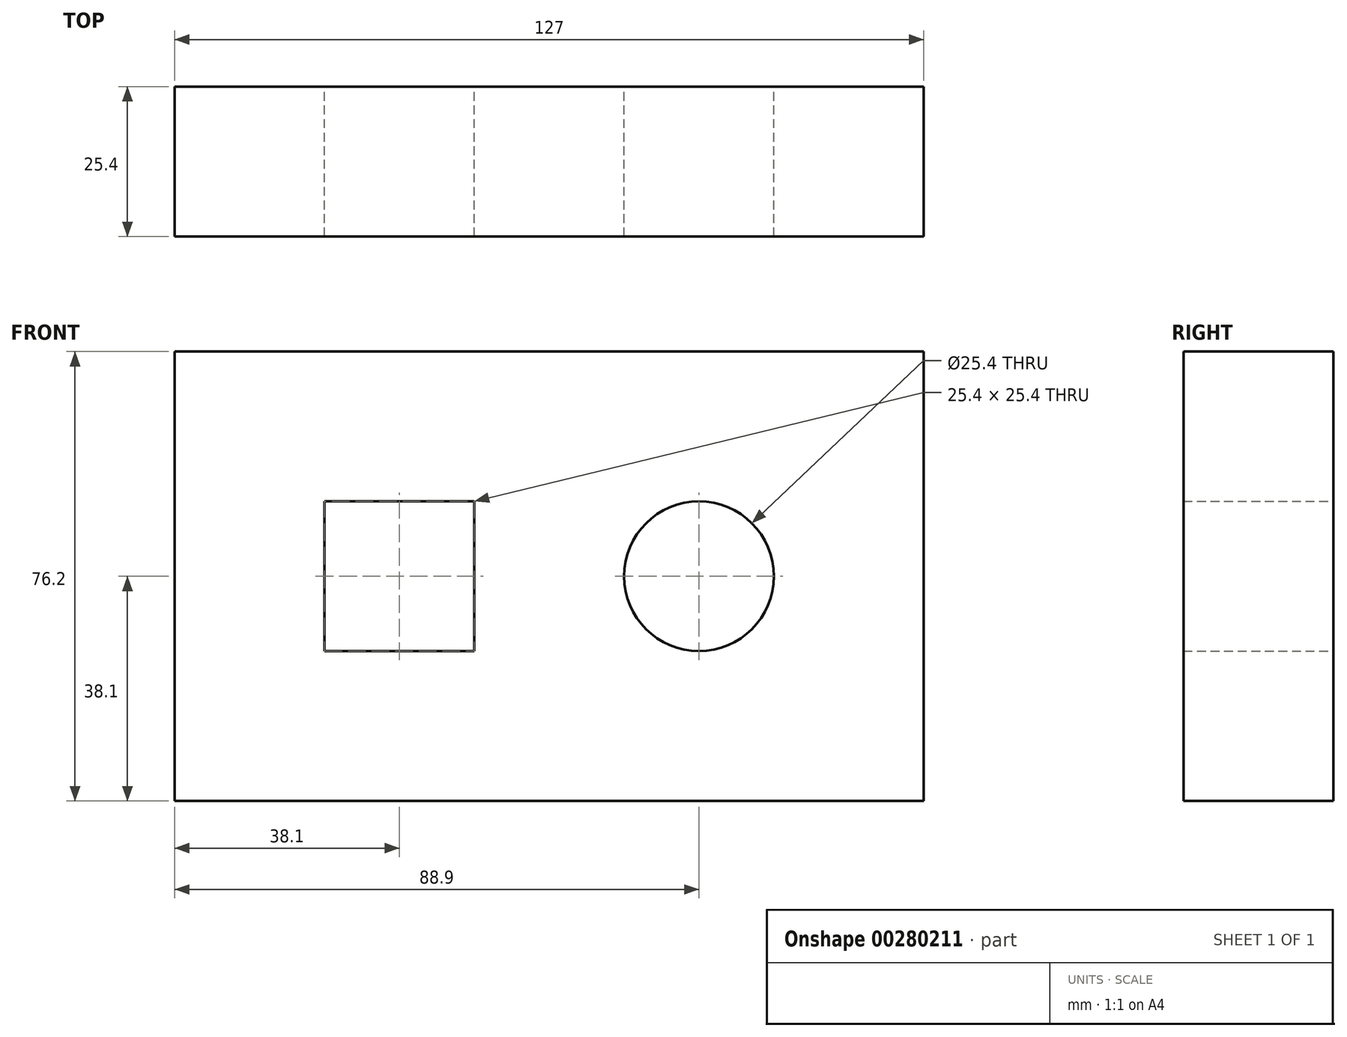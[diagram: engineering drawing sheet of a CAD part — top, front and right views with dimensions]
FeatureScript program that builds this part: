
annotation { "Feature Type Name" : "Feature", "Feature Type Description" : "" }
export const myFeature = defineFeature(function(context is Context, id is Id, definition is map)
    precondition{}
    {
        {
            var Q0;
            Q0=qCreatedBy(makeId("Front.planeOp"),FACE);
            var sketch = newSketch(context, id + "F0", { "sketchPlane" : qUnion([Q0])});
            skLineSegment(sketch, "E0.bottom", {"start": v(0, 0) * mm, "end": v(-127, 0) * mm});
            skLineSegment(sketch, "E0.top", {"start": v(0, 76.2) * mm, "end": v(-127, 76.2) * mm});
            skLineSegment(sketch, "E0.left", {"start": v(0, 0) * mm, "end": v(0, 76.2) * mm});
            skLineSegment(sketch, "E0.right", {"start": v(-127, 0) * mm, "end": v(-127, 76.2) * mm});
            skSolve(sketch);
        }
        {
            var Q0;
            Q0=makeQuery(id+"F0.imprint","IMPRINT",FACE,{"disambiguationData":[TD([[makeQuery(id+"F0.imprint","IMPRINT",EDGE,{"derivedFrom":sQuery(id+"F0.wireOp",EDGE,"E0.bottom")}),-1.0]])]});
            var sketch = newSketch(context, id + "F1", { "sketchPlane" : qUnion([Q0])});
            skLineSegment(sketch, "E1.bottom", {"start": v(-76.2, 50.8) * mm, "end": v(-101.6, 50.8) * mm});
            skLineSegment(sketch, "E1.top", {"start": v(-76.2, 25.4) * mm, "end": v(-101.6, 25.4) * mm});
            skLineSegment(sketch, "E1.left", {"start": v(-76.2, 50.8) * mm, "end": v(-76.2, 25.4) * mm});
            skLineSegment(sketch, "E1.right", {"start": v(-101.6, 50.8) * mm, "end": v(-101.6, 25.4) * mm});
            skSolve(sketch);
        }
        {
            var Q0;
            Q0=makeQuery(id+"F0.imprint","IMPRINT",FACE,{"disambiguationData":[TD([[makeQuery(id+"F0.imprint","IMPRINT",EDGE,{"derivedFrom":sQuery(id+"F0.wireOp",EDGE,"E0.bottom")}),-1.0]])]});
            var sketch = newSketch(context, id + "F2", { "sketchPlane" : qUnion([Q0])});
            skCircle(sketch, "E2", {"center": v(-38.1, 38.1) * mm, "radius": 12.7 * mm});
            skSolve(sketch);
        }
        {
            var Q0;
            Q0 = qSketchRegion(id + "F0", true);
            extrude(context, id + "F3", {"entities" : qUnion([Q0]), "depth" : 25.4 * mm});
        }
        {
            var Q0;
            Q0 = qSketchRegion(id + "F2", true);
            var Q1;
            Q1 = qSketchRegion(id + "F1", true);
            extrude(context, id + "F4", {"entities" : qUnion([Q0, Q1]), "operationType" : NewBodyOperationType.REMOVE, "depth" : 40.64 * mm});
        }
    });
